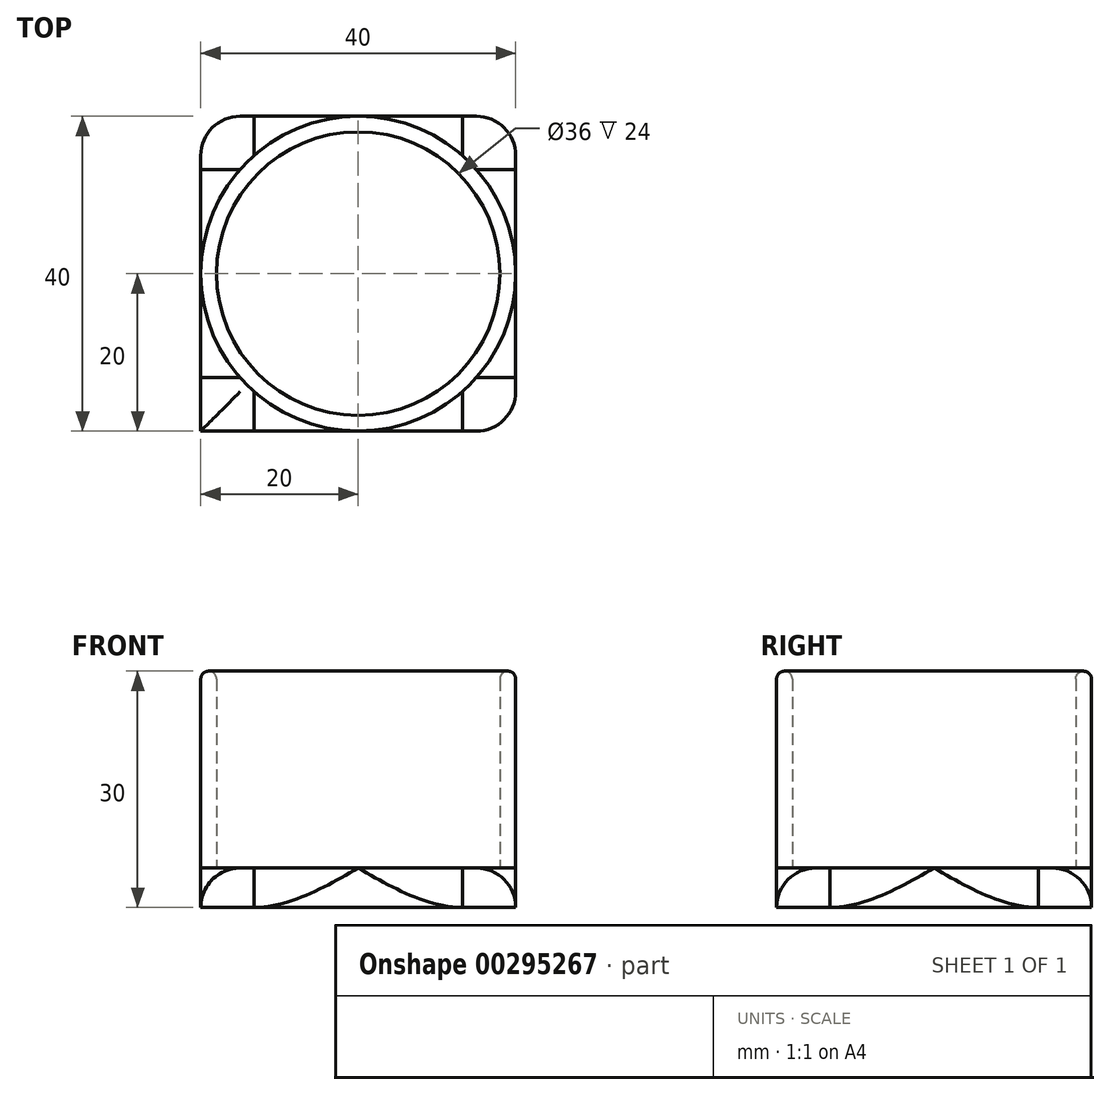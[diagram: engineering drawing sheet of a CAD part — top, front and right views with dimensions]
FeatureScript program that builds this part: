
annotation { "Feature Type Name" : "Feature", "Feature Type Description" : "" }
export const myFeature = defineFeature(function(context is Context, id is Id, definition is map)
    precondition{}
    {
        {
            var Q0;
            Q0=qCreatedBy(makeId("Top.planeOp"),FACE);
            var sketch = newSketch(context, id + "F0", { "sketchPlane" : qUnion([Q0])});
            skLineSegment(sketch, "E0.bottom", {"start": v(0, 0) * mm, "end": v(40, 0) * mm});
            skLineSegment(sketch, "E0.top", {"start": v(0, 40) * mm, "end": v(40, 40) * mm});
            skLineSegment(sketch, "E0.left", {"start": v(0, 0) * mm, "end": v(0, 40) * mm});
            skLineSegment(sketch, "E0.right", {"start": v(40, 0) * mm, "end": v(40, 40) * mm});
            skLineSegment(sketch, "E1.bottom", {"start": v(0, 0) * mm, "end": v(20, 0) * mm});
            skLineSegment(sketch, "E1.top", {"start": v(0, 20) * mm, "end": v(20, 20) * mm});
            skLineSegment(sketch, "E1.left", {"start": v(0, 0) * mm, "end": v(0, 20) * mm});
            skLineSegment(sketch, "E1.right", {"start": v(20, 0) * mm, "end": v(20, 20) * mm});
            skCircle(sketch, "E2", {"center": v(20, 20) * mm, "radius": 18 * mm});
            skCircle(sketch, "E3", {"center": v(20, 20) * mm, "radius": 20 * mm});
            skSolve(sketch);
        }
        {
            var Q0;
            {var subQ0=sQuery(id+"F0.wireOp",EDGE,"E0.top");Q0=makeQuery(id+"F0.imprint","IMPRINT",FACE,{"disambiguationData":[TD([[makeQuery(id+"F0.imprint","IMPRINT",EDGE,{"derivedFrom":subQ0}),-1.0]])]});}
            var Q1;
            {var subQ1=sQuery(id+"F0.wireOp",EDGE,"E1.top");var subQ3=sQuery(id+"F0.wireOp",EDGE,"E2");var subQ4=makeQuery(id+"F0.imprint","INTERSECT",VERTEX,{"derivedFrom":[subQ1,subQ3]});Q1=makeQuery(id+"F0.imprint","IMPRINT",FACE,{"disambiguationData":[TD([[makeQuery(id+"F0.imprint","IMPRINT",EDGE,{"disambiguationData":[TD([[subQ4,-1.0]])],"derivedFrom":subQ3}),-1.0]])]});}
            var Q2;
            {var subQ1=sQuery(id+"F0.wireOp",EDGE,"E1.top");var subQ4=sQuery(id+"F0.wireOp",EDGE,"E2");var subQ5=makeQuery(id+"F0.imprint","INTERSECT",VERTEX,{"derivedFrom":[subQ1,subQ4]});Q2=makeQuery(id+"F0.imprint","IMPRINT",FACE,{"disambiguationData":[TD([[makeQuery(id+"F0.imprint","IMPRINT",EDGE,{"disambiguationData":[TD([[subQ5,1.0]])],"derivedFrom":subQ4}),-1.0]])]});}
            var Q3;
            {var subQ0=sQuery(id+"F0.wireOp",EDGE,"E1.right");var subQ1=sQuery(id+"F0.wireOp",EDGE,"E1.top");var subQ2=makeQuery(id+"F0.imprint","INTERSECT",VERTEX,{"derivedFrom":[subQ1,subQ0]});Q3=makeQuery(id+"F0.imprint","IMPRINT",FACE,{"disambiguationData":[TD([[makeQuery(id+"F0.imprint","IMPRINT",EDGE,{"disambiguationData":[TD([[subQ2,1.0]])],"derivedFrom":subQ1}),1.0]])]});}
            var Q4;
            {var subQ0=sQuery(id+"F0.wireOp",EDGE,"E1.right");var subQ1=sQuery(id+"F0.wireOp",EDGE,"E1.top");var subQ2=makeQuery(id+"F0.imprint","INTERSECT",VERTEX,{"derivedFrom":[subQ1,subQ0]});Q4=makeQuery(id+"F0.imprint","IMPRINT",FACE,{"disambiguationData":[TD([[makeQuery(id+"F0.imprint","IMPRINT",EDGE,{"disambiguationData":[TD([[subQ2,1.0]])],"derivedFrom":subQ1}),-1.0]])]});}
            var Q5;
            {var subQ0=sQuery(id+"F0.wireOp",EDGE,"E1.bottom");Q5=makeQuery(id+"F0.imprint","IMPRINT",FACE,{"disambiguationData":[TD([[makeQuery(id+"F0.imprint","IMPRINT",EDGE,{"derivedFrom":subQ0}),1.0]])]});}
            var Q6;
            {var subQ0=sQuery(id+"F0.wireOp",EDGE,"E0.bottom");Q6=makeQuery(id+"F0.imprint","IMPRINT",FACE,{"disambiguationData":[TD([[makeQuery(id+"F0.imprint","IMPRINT",EDGE,{"derivedFrom":subQ0}),1.0]])]});}
            extrude(context, id + "F1", {"entities" : qUnion([Q0, Q1, Q2, Q3, Q4, Q5, Q6]), "depth" : 5 * mm, "offsetDistance" : 25 * mm});
        }
        {
            var Q0;
            {var subQ1=sQuery(id+"F0.wireOp",EDGE,"E1.top");var subQ3=sQuery(id+"F0.wireOp",EDGE,"E2");var subQ4=makeQuery(id+"F0.imprint","INTERSECT",VERTEX,{"derivedFrom":[subQ1,subQ3]});Q0=makeQuery(id+"F0.imprint","IMPRINT",FACE,{"disambiguationData":[TD([[makeQuery(id+"F0.imprint","IMPRINT",EDGE,{"disambiguationData":[TD([[subQ4,-1.0]])],"derivedFrom":subQ3}),-1.0]])]});}
            var Q1;
            {var subQ1=sQuery(id+"F0.wireOp",EDGE,"E1.top");var subQ4=sQuery(id+"F0.wireOp",EDGE,"E2");var subQ5=makeQuery(id+"F0.imprint","INTERSECT",VERTEX,{"derivedFrom":[subQ1,subQ4]});Q1=makeQuery(id+"F0.imprint","IMPRINT",FACE,{"disambiguationData":[TD([[makeQuery(id+"F0.imprint","IMPRINT",EDGE,{"disambiguationData":[TD([[subQ5,1.0]])],"derivedFrom":subQ4}),-1.0]])]});}
            extrude(context, id + "F2", {"entities" : qUnion([Q0, Q1]), "operationType" : NewBodyOperationType.ADD, "depth" : 30 * mm});
        }
        {
            var Q0;
            Q0=makeQuery(id+"F2.opExtrude","CAP_EDGE",EDGE,{"disambiguationData":[OSD([sQuery(id+"F0.wireOp",EDGE,"E3")])],"isStart":false});
            var Q1;
            Q1=makeQuery(id+"F2.opExtrude","CAP_EDGE",EDGE,{"disambiguationData":[OSD([sQuery(id+"F0.wireOp",EDGE,"E2")])],"isStart":false});
            fillet(context, id + "F3", {"entities" : qUnion([Q0, Q1]), "radius" : 1 * mm, "tangentPropagation" : true, "allowEdgeOverflow" : false});
        }
        {
            var Q0;
            Q0=makeQuery(id+"F1.opExtrude","SWEPT_EDGE",EDGE,{"disambiguationData":[OSD([sQuery(id+"F0.wireOp",EDGE,"E1.bottom"),sQuery(id+"F0.wireOp",EDGE,"E1.left")])]});
            var Q1;
            Q1=makeQuery(id+"F1.opExtrude","SWEPT_EDGE",EDGE,{"disambiguationData":[OSD([sQuery(id+"F0.wireOp",EDGE,"E0.bottom"),sQuery(id+"F0.wireOp",EDGE,"E0.right")])]});
            var Q2;
            Q2=makeQuery(id+"F1.opExtrude","SWEPT_EDGE",EDGE,{"disambiguationData":[OSD([sQuery(id+"F0.wireOp",EDGE,"E0.top"),sQuery(id+"F0.wireOp",EDGE,"E0.right")])]});
            var Q3;
            Q3=makeQuery(id+"F1.opExtrude","SWEPT_EDGE",EDGE,{"disambiguationData":[OSD([sQuery(id+"F0.wireOp",EDGE,"E0.top"),sQuery(id+"F0.wireOp",EDGE,"E0.left")])]});
            var Q4;
            {var subQ0=sQuery(id+"F0.wireOp",EDGE,"E1.left");var subQ1=sQuery(id+"F0.wireOp",EDGE,"E0.left");var subQ2=sQuery(id+"F0.wireOp",EDGE,"E0.top");Q4=makeQuery(id+"F2.boolean.opBoolean","SPLIT",EDGE,{"disambiguationData":[TD([makeQuery(id+"F1.opExtrude","SWEPT_FACE",FACE,{"disambiguationData":[OSD([subQ2])]})])],"derivedFrom":makeQuery(id+"F1.opExtrude","CAP_EDGE",EDGE,{"disambiguationData":[OSD([subQ1,subQ0])],"isStart":false})});}
            var Q5;
            {var subQ0=sQuery(id+"F0.wireOp",EDGE,"E1.left");var subQ1=sQuery(id+"F0.wireOp",EDGE,"E1.bottom");var subQ2=sQuery(id+"F0.wireOp",EDGE,"E0.left");var subQ3=sQuery(id+"F0.wireOp",EDGE,"E0.bottom");Q5=makeQuery(id+"F2.boolean.opBoolean","SPLIT",EDGE,{"disambiguationData":[TD([makeQuery(id+"F1.opExtrude","SWEPT_FACE",FACE,{"disambiguationData":[OSD([subQ3,subQ1])]})])],"derivedFrom":makeQuery(id+"F1.opExtrude","CAP_EDGE",EDGE,{"disambiguationData":[OSD([subQ2,subQ0])],"isStart":false})});}
            var Q6;
            {var subQ0=sQuery(id+"F0.wireOp",EDGE,"E1.left");var subQ1=sQuery(id+"F0.wireOp",EDGE,"E0.left");var subQ2=sQuery(id+"F0.wireOp",EDGE,"E0.top");Q6=makeQuery(id+"F2.boolean.opBoolean","SPLIT",EDGE,{"disambiguationData":[TD([makeQuery(id+"F1.opExtrude","SWEPT_FACE",FACE,{"disambiguationData":[OSD([subQ1,subQ0])]})])],"derivedFrom":makeQuery(id+"F1.opExtrude","CAP_EDGE",EDGE,{"disambiguationData":[OSD([subQ2])],"isStart":false})});}
            var Q7;
            {var subQ0=sQuery(id+"F0.wireOp",EDGE,"E0.right");var subQ1=sQuery(id+"F0.wireOp",EDGE,"E0.top");Q7=makeQuery(id+"F2.boolean.opBoolean","SPLIT",EDGE,{"disambiguationData":[TD([makeQuery(id+"F1.opExtrude","SWEPT_FACE",FACE,{"disambiguationData":[OSD([subQ1])]})])],"derivedFrom":makeQuery(id+"F1.opExtrude","CAP_EDGE",EDGE,{"disambiguationData":[OSD([subQ0])],"isStart":false})});}
            var Q8;
            {var subQ0=sQuery(id+"F0.wireOp",EDGE,"E1.left");var subQ1=sQuery(id+"F0.wireOp",EDGE,"E1.bottom");var subQ2=sQuery(id+"F0.wireOp",EDGE,"E0.left");var subQ3=sQuery(id+"F0.wireOp",EDGE,"E0.bottom");Q8=makeQuery(id+"F2.boolean.opBoolean","SPLIT",EDGE,{"disambiguationData":[TD([makeQuery(id+"F1.opExtrude","SWEPT_FACE",FACE,{"disambiguationData":[OSD([subQ2,subQ0])]})])],"derivedFrom":makeQuery(id+"F1.opExtrude","CAP_EDGE",EDGE,{"disambiguationData":[OSD([subQ3,subQ1])],"isStart":false})});}
            fillet(context, id + "F4", {"entities" : qUnion([Q0, Q1, Q2, Q3, Q4, Q5, Q6, Q7, Q8]), "radius" : 5 * mm, "tangentPropagation" : true, "allowEdgeOverflow" : false});
        }
    });
